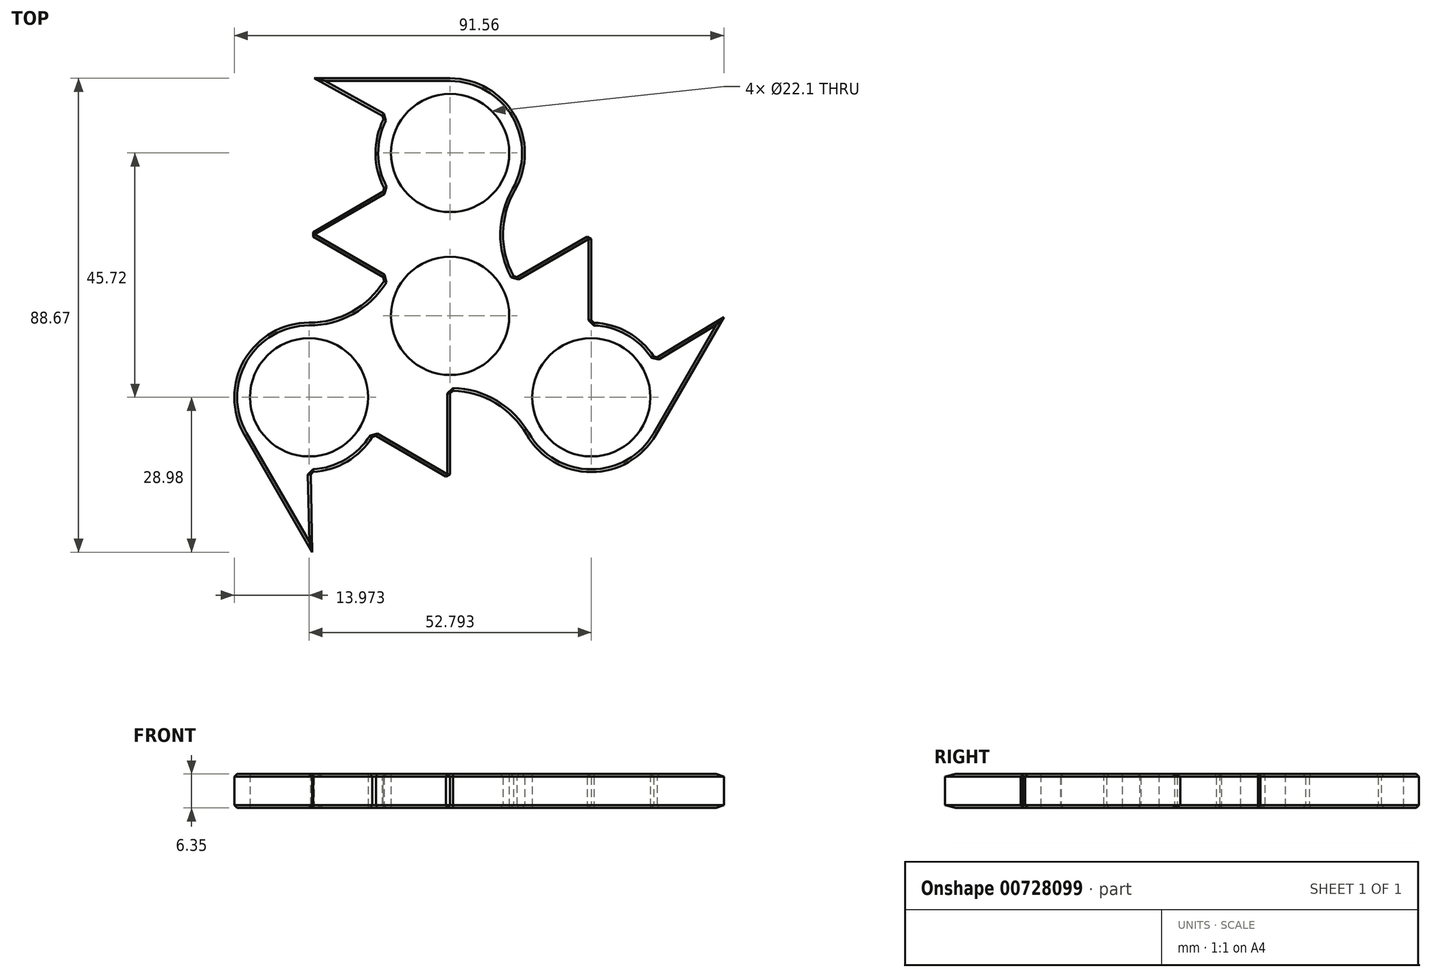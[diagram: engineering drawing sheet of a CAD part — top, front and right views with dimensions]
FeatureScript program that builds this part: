
annotation { "Feature Type Name" : "Feature", "Feature Type Description" : "" }
export const myFeature = defineFeature(function(context is Context, id is Id, definition is map)
    precondition{}
    {
        {
            var Q0;
            Q0=qCreatedBy(makeId("Top.planeOp"),FACE);
            var sketch = newSketch(context, id + "F0", { "sketchPlane" : qUnion([Q0])});
            skCircle(sketch, "E0", {"center": v(0, 0) * mm, "radius": 11.05 * mm});
            skCircle(sketch, "E1", {"center": v(0, 0) * mm, "radius": 13.97 * mm});
            skLineSegment(sketch, "E2", {"start": v(0, 0) * mm, "end": v(0, 30.48) * mm});
            skCircle(sketch, "E3", {"center": v(0, 30.48) * mm, "radius": 11.05 * mm});
            skCircle(sketch, "E4", {"center": v(0, 30.48) * mm, "radius": 13.97 * mm});
            skCircle(sketch, "E5.1.0", {"center": v(-26.4, -15.24) * mm, "radius": 13.97 * mm});
            skCircle(sketch, "E5.1.1", {"center": v(-26.4, -15.24) * mm, "radius": 11.05 * mm});
            skCircle(sketch, "E5.2.0", {"center": v(26.4, -15.24) * mm, "radius": 13.97 * mm});
            skCircle(sketch, "E5.2.1", {"center": v(26.4, -15.24) * mm, "radius": 11.05 * mm});
            skArc(sketch, "E6", {"start": v(-26.4, -1.27) * mm, "mid": v(-14.63, 3.66) * mm, "end": v(-9.89, 15.5) * mm});
            skArc(sketch, "E7.1.0", {"start": v(14.3, -22.23) * mm, "mid": v(0, -13.97) * mm, "end": v(-14.3, -22.23) * mm});
            skArc(sketch, "E7.2.0", {"start": v(12.1, 23.5) * mm, "mid": v(12.1, 6.98) * mm, "end": v(26.4, -1.27) * mm});
            skPoint(sketch, "E8.endSnap0", {"position": v(0, 15.24) * mm});
            skLineSegment(sketch, "E9", {"start": v(-14.3, -22.23) * mm, "end": v(0, -30.48) * mm});
            skLineSegment(sketch, "E10", {"start": v(0, 0) * mm, "end": v(0, -30.48) * mm});
            skLineSegment(sketch, "E11", {"start": v(-12.1, 23.5) * mm, "end": v(-26.4, 15.24) * mm});
            skLineSegment(sketch, "E12", {"start": v(-26.4, 15.24) * mm, "end": v(-26.17, 15.1) * mm});
            skLineSegment(sketch, "E13", {"start": v(26.4, -1.27) * mm, "end": v(26.4, 15.24) * mm});
            skLineSegment(sketch, "E14", {"start": v(0, 0) * mm, "end": v(26.4, 15.24) * mm});
            skLineSegment(sketch, "E15", {"start": v(0, 30.48) * mm, "end": v(0, 44.45) * mm});
            skLineSegment(sketch, "E16", {"start": v(0, 44.45) * mm, "end": v(-25.4, 44.45) * mm});
            skLineSegment(sketch, "E17", {"start": v(-25.4, 44.45) * mm, "end": v(0, 30.48) * mm});
            skLineSegment(sketch, "E18.1.0", {"start": v(-38.5, -22.22) * mm, "end": v(-25.8, -44.22) * mm});
            skLineSegment(sketch, "E18.1.1", {"start": v(-25.8, -44.22) * mm, "end": v(-26.4, -15.24) * mm});
            skLineSegment(sketch, "E18.2.0", {"start": v(38.5, -22.23) * mm, "end": v(51.2, -0.23) * mm});
            skLineSegment(sketch, "E18.2.1", {"start": v(51.2, -0.23) * mm, "end": v(26.4, -15.24) * mm});
            skLineSegment(sketch, "E19", {"start": v(-26.17, 15.1) * mm, "end": v(0, 0) * mm});
            skArc(sketch, "E20", {"start": v(-9.89, 15.5) * mm, "mid": v(-10.48, 19.64) * mm, "end": v(-12.1, 23.5) * mm});
            skSolve(sketch);
        }
        {
            var Q0;
            Q0 = qSketchRegion(id + "F0", true);
            extrude(context, id + "F1", {"entities" : qUnion([Q0]), "depth" : 6.35 * mm, "offsetDistance" : 25.4 * mm});
        }
        {
            var Q0;
            {var subQ0=sQuery(id+"F0.wireOp",EDGE,"E5.1.0");Q0=makeQuery(id+"F1.opExtrude","SWEPT_FACE",FACE,{"disambiguationData":[OSD([subQ0]),TDD([makeQuery(id+"F0.imprint","IMPRINT",EDGE,{"disambiguationData":[TD([[makeQuery(id+"F0.imprint","INTERSECT",VERTEX,{"derivedFrom":[subQ0,sQuery(id+"F0.wireOp",EDGE,"db4dc759-b9bd-4eb0-ab5e-a3482fc2fdc1.1.0")]}),-1.0]])],"derivedFrom":subQ0})])]});}
            var Q1;
            Q1=makeQuery(id+"F1.opExtrude","SWEPT_FACE",FACE,{"disambiguationData":[OSD([sQuery(id+"F0.wireOp",EDGE,"E9")])]});
            var Q2;
            Q2=makeQuery(id+"F1.opExtrude","CAP_EDGE",EDGE,{"disambiguationData":[OSD([sQuery(id+"F0.wireOp",EDGE,"db4dc759-b9bd-4eb0-ab5e-a3482fc2fdc1.1.1")])],"isStart":false});
            var Q3;
            Q3=makeQuery(id+"F1.opExtrude","CAP_EDGE",EDGE,{"disambiguationData":[OSD([sQuery(id+"F0.wireOp",EDGE,"db4dc759-b9bd-4eb0-ab5e-a3482fc2fdc1.1.1")])],"isStart":true});
            var Q4;
            Q4=makeQuery(id+"F1.opExtrude","SWEPT_FACE",FACE,{"disambiguationData":[OSD([sQuery(id+"F0.wireOp",EDGE,"E7.1.0")])]});
            var Q5;
            Q5=makeQuery(id+"F1.opExtrude","SWEPT_FACE",FACE,{"disambiguationData":[OSD([sQuery(id+"F0.wireOp",EDGE,"E7.2.0")])]});
            var Q6;
            {var subQ0=sQuery(id+"F0.wireOp",EDGE,"E4");Q6=makeQuery(id+"F1.opExtrude","SWEPT_FACE",FACE,{"disambiguationData":[OSD([subQ0]),TDD([makeQuery(id+"F0.imprint","IMPRINT",EDGE,{"disambiguationData":[TD([[makeQuery(id+"F0.imprint","INTERSECT",VERTEX,{"derivedFrom":[subQ0,sQuery(id+"F0.wireOp",EDGE,"E7.2.0")]}),-1.0]])],"derivedFrom":subQ0})])]});}
            var Q7;
            Q7=makeQuery(id+"F1.opExtrude","SWEPT_FACE",FACE,{"disambiguationData":[OSD([sQuery(id+"F0.wireOp",EDGE,"E13")])]});
            var Q8;
            {var subQ0=sQuery(id+"F0.wireOp",EDGE,"E5.2.0");Q8=makeQuery(id+"F1.opExtrude","SWEPT_FACE",FACE,{"disambiguationData":[OSD([subQ0]),TDD([makeQuery(id+"F0.imprint","IMPRINT",EDGE,{"disambiguationData":[TD([[makeQuery(id+"F0.imprint","INTERSECT",VERTEX,{"derivedFrom":[subQ0,sQuery(id+"F0.wireOp",EDGE,"db4dc759-b9bd-4eb0-ab5e-a3482fc2fdc1.2.0")]}),-1.0]])],"derivedFrom":subQ0})])]});}
            var Q9;
            Q9=makeQuery(id+"F1.opExtrude","SWEPT_FACE",FACE,{"disambiguationData":[OSD([sQuery(id+"F0.wireOp",EDGE,"db4dc759-b9bd-4eb0-ab5e-a3482fc2fdc1.2.1")])]});
            var Q10;
            Q10=makeQuery(id+"F1.opExtrude","SWEPT_FACE",FACE,{"disambiguationData":[OSD([sQuery(id+"F0.wireOp",EDGE,"db4dc759-b9bd-4eb0-ab5e-a3482fc2fdc1.2.0")])]});
            var Q11;
            Q11=makeQuery(id+"F1.opExtrude","SWEPT_FACE",FACE,{"disambiguationData":[OSD([sQuery(id+"F0.wireOp",EDGE,"E14")])]});
            var Q12;
            {var subQ0=sQuery(id+"F0.wireOp",EDGE,"E5.2.0");Q12=makeQuery(id+"F1.opExtrude","SWEPT_FACE",FACE,{"disambiguationData":[OSD([subQ0]),TDD([makeQuery(id+"F0.imprint","IMPRINT",EDGE,{"disambiguationData":[TD([[makeQuery(id+"F0.imprint","INTERSECT",VERTEX,{"derivedFrom":[subQ0,sQuery(id+"F0.wireOp",EDGE,"E7.1.0")]}),-1.0]])],"derivedFrom":subQ0})])]});}
            var Q13;
            Q13=makeQuery(id+"F1.opExtrude","SWEPT_FACE",FACE,{"disambiguationData":[OSD([sQuery(id+"F0.wireOp",EDGE,"E10")])]});
            var Q14;
            Q14=makeQuery(id+"F1.opExtrude","SWEPT_FACE",FACE,{"disambiguationData":[OSD([sQuery(id+"F0.wireOp",EDGE,"db4dc759-b9bd-4eb0-ab5e-a3482fc2fdc1.1.0")])]});
            var Q15;
            {var subQ0=sQuery(id+"F0.wireOp",EDGE,"E5.1.0");Q15=makeQuery(id+"F1.opExtrude","SWEPT_FACE",FACE,{"disambiguationData":[OSD([subQ0]),TDD([makeQuery(id+"F0.imprint","IMPRINT",EDGE,{"disambiguationData":[TD([[makeQuery(id+"F0.imprint","INTERSECT",VERTEX,{"derivedFrom":[subQ0,sQuery(id+"F0.wireOp",EDGE,"E6")]}),-1.0]])],"derivedFrom":subQ0})])]});}
            var Q16;
            Q16=makeQuery(id+"F1.opExtrude","SWEPT_FACE",FACE,{"disambiguationData":[OSD([sQuery(id+"F0.wireOp",EDGE,"DN0Bj1Ua-UzeU-aU5S-2e2i-ZLfPcYhDtTPj")])]});
            var Q17;
            Q17=makeQuery(id+"F1.opExtrude","SWEPT_FACE",FACE,{"disambiguationData":[OSD([sQuery(id+"F0.wireOp",EDGE,"E11")])]});
            var Q18;
            Q18=makeQuery(id+"F1.opExtrude","SWEPT_FACE",FACE,{"disambiguationData":[OSD([sQuery(id+"F0.wireOp",EDGE,"E6")])]});
            var Q19;
            Q19=makeQuery(id+"F1.opExtrude","SWEPT_FACE",FACE,{"disambiguationData":[OSD([sQuery(id+"F0.wireOp",EDGE,"E12")])]});
            var Q20;
            Q20=makeQuery(id+"F1.opExtrude","SWEPT_FACE",FACE,{"disambiguationData":[OSD([sQuery(id+"F0.wireOp",EDGE,"VQRhF502-ECMC-4loj-9c3v-dmIcGu2boxO4")])]});
            var Q21;
            {var subQ0=sQuery(id+"F0.wireOp",EDGE,"E4");Q21=makeQuery(id+"F1.opExtrude","SWEPT_FACE",FACE,{"disambiguationData":[OSD([subQ0]),TDD([makeQuery(id+"F0.imprint","IMPRINT",EDGE,{"disambiguationData":[TD([[makeQuery(id+"F0.imprint","INTERSECT",VERTEX,{"derivedFrom":[subQ0,sQuery(id+"F0.wireOp",EDGE,"VQRhF502-ECMC-4loj-9c3v-dmIcGu2boxO4")]}),-1.0]])],"derivedFrom":subQ0})])]});}
            chamfer(context, id + "F2", {"entities" : qUnion([Q0, Q1, Q2, Q3, Q4, Q5, Q6, Q7, Q8, Q9, Q10, Q11, Q12, Q13, Q14, Q15, Q16, Q17, Q18, Q19, Q20, Q21]), "width" : 0.5 * mm, "tangentPropagation" : true});
        }
    });
